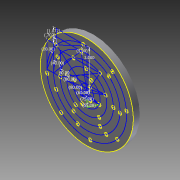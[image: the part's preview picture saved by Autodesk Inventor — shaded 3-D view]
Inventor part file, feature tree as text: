
AUTODESK INVENTOR PART (.ipt)
format: ipt  version: 2012 (Build 160160000, 160)  size: 189,440 bytes
history: native  units: in
note: dims shown in document units (in); Inventor stores cm internally (conversion verified against a paired STEP export)
features: sketch x2, extrude x1, hole x1
ambient origin geometry x8: Origin, YZ Plane, XZ Plane, XY Plane, X Axis, Y Axis, Z Axis, Center Point
feature tree (4):
  sketch  "Sketch3"  dims[d104=0.5in d105=0.5in]
  extrude  "Extrusion3"  Depth=0.5in
  hole  "Hole2"  [1 undecoded]
  sketch  "Sketch5"  dims[d106=0.5in d107=0.5in d108=0.5in d110=1.0in d111=0.2749in d112=0.2749in d113=0.2749in d114=0.2749in d115=0.2749in d116=3.1496in d118=360.0deg d120=2.7559in d122=360.0deg d124=2.3622in d126=360.0deg d128=1.9685in d130=360.0deg d132=1.5748in d134=360.0deg d136=1.1811in d138=360.0deg d140=0.5in d141=0.5in d142=0.0in d143=0.25in d144=0.75in d145=0.375in d146=0.25in d147=0.5635in d148=1.0in d149=0.8108in d155=0.1374in d156=0.2749in d157=60.0deg d158=0.5497in d159=0.5497in d160=60.0deg d161=3.0in d172=0.3779in d173=75.0deg d174=0.0344in d175=1.0716in d176=0.7019in]
note: 1 required parameter value undecoded (feature->parameter linkage not recoverable at this tier; creation-order binding heuristic only, values carry confidence <= 0.55)
